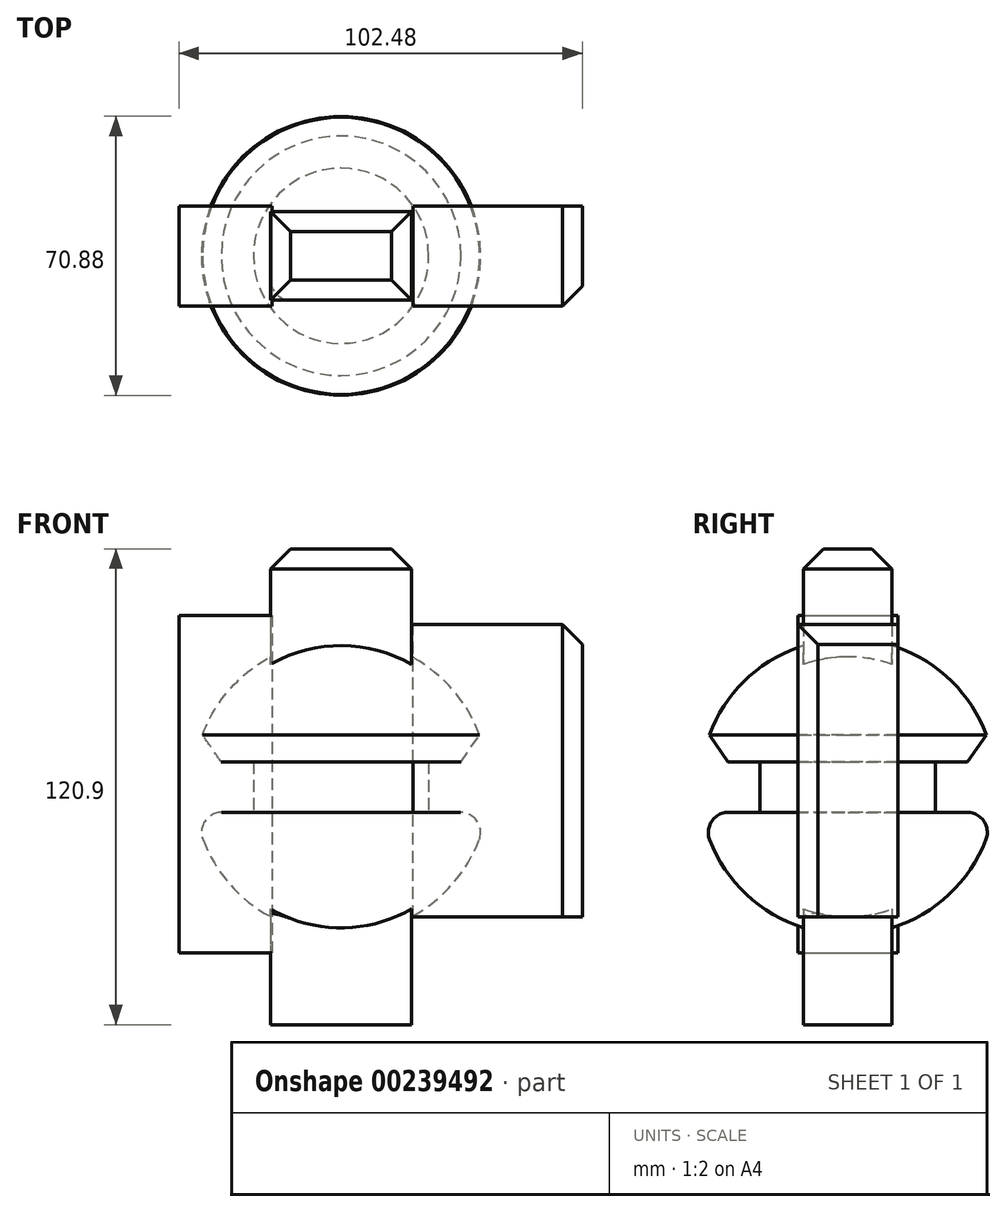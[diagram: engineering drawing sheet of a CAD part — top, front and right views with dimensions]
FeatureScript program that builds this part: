
annotation { "Feature Type Name" : "Feature", "Feature Type Description" : "" }
export const myFeature = defineFeature(function(context is Context, id is Id, definition is map)
    precondition{}
    {
        {
            var Q0;
            Q0=qCreatedBy(makeId("Front.planeOp"),FACE);
            var sketch = newSketch(context, id + "F0", { "sketchPlane" : qUnion([Q0])});
            skArc(sketch, "E0", {"start": v(0, -37.58) * mm, "mid": v(37.58, 0) * mm, "end": v(0, 37.58) * mm});
            skLineSegment(sketch, "E1", {"start": v(0, 37.58) * mm, "end": v(0, -37.58) * mm});
            skSolve(sketch);
        }
        {
            var Q0;
            Q0 = qSketchRegion(id + "F0", true);
            var Q1;
            Q1=sQuery(id+"F0.wireOp",EDGE,"E1");
            revolve(context, id + "F1", {"entities" : qUnion([Q0]), "axis" : qUnion([Q1]), "revolveType" : RevolveType.FULL});
        }
        {
            var Q0;
            Q0=qCreatedBy(makeId("Front.planeOp"),FACE);
            var sketch = newSketch(context, id + "F2", { "sketchPlane" : qUnion([Q0])});
            skLineSegment(sketch, "E2.bottom", {"start": v(22.27, -6.5) * mm, "end": v(50.26, -6.5) * mm});
            skLineSegment(sketch, "E2.top", {"start": v(22.27, 6.3) * mm, "end": v(50.26, 6.3) * mm});
            skLineSegment(sketch, "E2.left", {"start": v(22.27, -6.5) * mm, "end": v(22.27, 6.3) * mm});
            skLineSegment(sketch, "E2.right", {"start": v(50.26, -6.5) * mm, "end": v(50.26, 6.3) * mm});
            skLineSegment(sketch, "E3", {"start": v(0, 37.84) * mm, "end": v(0, -36.65) * mm});
            skSolve(sketch);
        }
        {
            var Q0;
            Q0 = qSketchRegion(id + "F2", true);
            var Q1;
            Q1=sQuery(id+"F2.wireOp",EDGE,"E3");
            revolve(context, id + "F3", {"operationType" : NewBodyOperationType.REMOVE, "entities" : qUnion([Q0]), "axis" : qUnion([Q1]), "revolveType" : RevolveType.FULL, "oppositeDirection" : true});
        }
        {
            var Q0;
            Q0=qCreatedBy(makeId("Top.planeOp"),FACE);
            var sketch = newSketch(context, id + "F4", { "sketchPlane" : qUnion([Q0])});
            skLineSegment(sketch, "E4.bottom", {"start": v(17.93, 11.23) * mm, "end": v(-17.93, 11.23) * mm});
            skLineSegment(sketch, "E4.top", {"start": v(17.93, -11.23) * mm, "end": v(-17.93, -11.23) * mm});
            skLineSegment(sketch, "E4.left", {"start": v(17.93, 11.23) * mm, "end": v(17.93, -11.23) * mm});
            skLineSegment(sketch, "E4.right", {"start": v(-17.93, 11.23) * mm, "end": v(-17.93, -11.23) * mm});
            skPoint(sketch, "E4.middle", {"position": v(0, 0) * mm});
            skSolve(sketch);
        }
        {
            var Q0;
            Q0 = qSketchRegion(id + "F4", true);
            extrude(context, id + "F5", {"entities" : qUnion([Q0]), "operationType" : NewBodyOperationType.ADD, "endBound" : BoundingType.SYMMETRIC, "depth" : 120.9 * mm});
        }
        {
            var Q0;
            Q0=makeQuery(id+"F5.opExtrude","CAP_EDGE",EDGE,{"disambiguationData":[OSD([sQuery(id+"F4.wireOp",EDGE,"E4.left")])],"isStart":false});
            chamfer(context, id + "F6", {"entities" : qUnion([Q0]), "width" : 5.08 * mm, "tangentPropagation" : true});
        }
        {
            var Q0;
            Q0=makeQuery(id+"F5.opExtrude","CAP_EDGE",EDGE,{"disambiguationData":[OSD([sQuery(id+"F4.wireOp",EDGE,"E4.right")])],"isStart":false});
            chamfer(context, id + "F7", {"entities" : qUnion([Q0]), "width" : 5.08 * mm, "tangentPropagation" : true});
        }
        {
            var Q0;
            Q0=makeQuery(id+"F5.opExtrude","CAP_EDGE",EDGE,{"disambiguationData":[OSD([sQuery(id+"F4.wireOp",EDGE,"E4.top")])],"isStart":false});
            chamfer(context, id + "F8", {"entities" : qUnion([Q0]), "width" : 5.08 * mm, "tangentPropagation" : true});
        }
        {
            var Q0;
            Q0=makeQuery(id+"F5.opExtrude","CAP_EDGE",EDGE,{"disambiguationData":[OSD([sQuery(id+"F4.wireOp",EDGE,"E4.bottom")])],"isStart":false});
            chamfer(context, id + "F9", {"entities" : qUnion([Q0]), "width" : 5.08 * mm, "tangentPropagation" : true});
        }
        {
            var Q0;
            Q0=makeQuery(id+"F3.boolean.opBoolean","INTERSECT",EDGE,{"derivedFrom":[makeQuery(id+"F1.opRevolve","SWEPT_FACE",FACE,{"disambiguationData":[OSD([sQuery(id+"F0.wireOp",EDGE,"E0")])]}),makeQuery(id+"F3.opRevolve","SWEPT_FACE",FACE,{"disambiguationData":[OSD([sQuery(id+"F2.wireOp",EDGE,"E2.top")])]})]});
            chamfer(context, id + "F10", {"entities" : qUnion([Q0]), "width" : 5.08 * mm, "tangentPropagation" : true});
        }
        {
            var Q0;
            Q0=makeQuery(id+"F3.boolean.opBoolean","INTERSECT",EDGE,{"derivedFrom":[makeQuery(id+"F1.opRevolve","SWEPT_FACE",FACE,{"disambiguationData":[OSD([sQuery(id+"F0.wireOp",EDGE,"E0")])]}),makeQuery(id+"F3.opRevolve","SWEPT_FACE",FACE,{"disambiguationData":[OSD([sQuery(id+"F2.wireOp",EDGE,"E2.bottom")])]})]});
            fillet(context, id + "F11", {"entities" : qUnion([Q0]), "radius" : 5.08 * mm, "tangentPropagation" : true, "allowEdgeOverflow" : false});
        }
        {
            var Q0;
            {var subQ0=sQuery(id+"F4.wireOp",EDGE,"E4.right");var subQ1=sQuery(id+"F4.wireOp",EDGE,"E4.top");Q0=makeQuery(id+"F5.boolean.opBoolean","SPLIT",EDGE,{"disambiguationData":[TD([makeQuery(id+"F5.opExtrude","CAP_FACE",FACE,{"disambiguationData":[OSD([sQuery(id+"F4.wireOp",EDGE,"E4.bottom"),subQ1,sQuery(id+"F4.wireOp",EDGE,"E4.left"),subQ0])],"isStart":true})])],"derivedFrom":makeQuery(id+"F5.opExtrude","SWEPT_EDGE",EDGE,{"disambiguationData":[OSD([subQ1,subQ0])]})});}
            fillet(context, id + "F12", {"entities" : qUnion([Q0]), "radius" : 5.08 * mm, "tangentPropagation" : true, "allowEdgeOverflow" : false});
        }
        {
            var Q0;
            Q0=qCreatedBy(makeId("Front.planeOp"),FACE);
            var sketch = newSketch(context, id + "F13", { "sketchPlane" : qUnion([Q0])});
            skLineSegment(sketch, "E5.bottom", {"start": v(-17.54, 43.55) * mm, "end": v(-41.19, 43.55) * mm});
            skLineSegment(sketch, "E5.top", {"start": v(-17.54, -42.17) * mm, "end": v(-41.19, -42.17) * mm});
            skLineSegment(sketch, "E5.left", {"start": v(-17.54, 43.55) * mm, "end": v(-17.54, -42.17) * mm});
            skLineSegment(sketch, "E5.right", {"start": v(-41.19, 43.55) * mm, "end": v(-41.19, -42.17) * mm});
            skSolve(sketch);
        }
        {
            var Q0;
            Q0 = qSketchRegion(id + "F13", true);
            extrude(context, id + "F14", {"entities" : qUnion([Q0]), "endBound" : BoundingType.SYMMETRIC, "depth" : 25.4 * mm});
        }
        {
            var Q0;
            Q0=qCreatedBy(makeId("Front.planeOp"),FACE);
            var sketch = newSketch(context, id + "F15", { "sketchPlane" : qUnion([Q0])});
            skLineSegment(sketch, "E6.bottom", {"start": v(18.33, -33.1) * mm, "end": v(61.29, -33.1) * mm});
            skLineSegment(sketch, "E6.top", {"start": v(18.33, 41.19) * mm, "end": v(61.29, 41.19) * mm});
            skLineSegment(sketch, "E6.left", {"start": v(18.33, -33.1) * mm, "end": v(18.33, 41.19) * mm});
            skLineSegment(sketch, "E6.right", {"start": v(61.29, -33.1) * mm, "end": v(61.29, 41.19) * mm});
            skSolve(sketch);
        }
        {
            var Q0;
            Q0 = qSketchRegion(id + "F15", true);
            extrude(context, id + "F16", {"entities" : qUnion([Q0]), "endBound" : BoundingType.SYMMETRIC, "depth" : 25.4 * mm});
        }
        {
            var Q0;
            Q0=makeQuery(id+"F16.opExtrude","SWEPT_EDGE",EDGE,{"disambiguationData":[OSD([sQuery(id+"F15.wireOp",EDGE,"E6.top"),sQuery(id+"F15.wireOp",EDGE,"E6.right")])]});
            chamfer(context, id + "F17", {"entities" : qUnion([Q0]), "width" : 5.08 * mm, "tangentPropagation" : true});
        }
        {
            var Q0;
            Q0=makeQuery(id+"F16.opExtrude","CAP_EDGE",EDGE,{"disambiguationData":[OSD([sQuery(id+"F15.wireOp",EDGE,"E6.right")])],"isStart":false});
            chamfer(context, id + "F18", {"entities" : qUnion([Q0]), "width" : 5.08 * mm, "tangentPropagation" : true});
        }
    });
